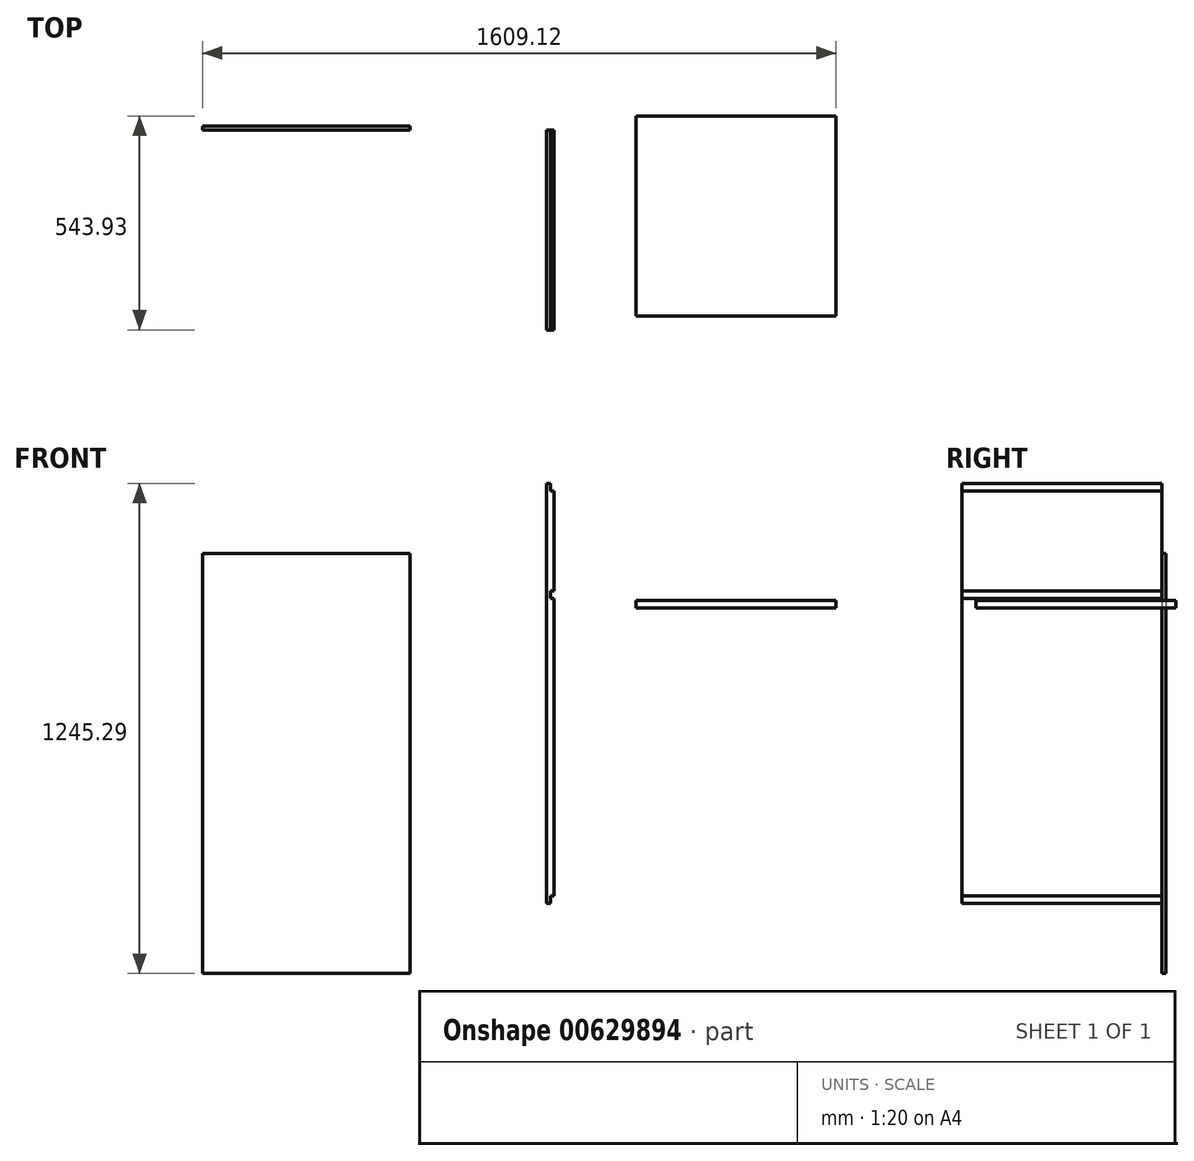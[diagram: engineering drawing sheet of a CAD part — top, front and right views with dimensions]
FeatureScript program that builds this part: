
annotation { "Feature Type Name" : "Feature", "Feature Type Description" : "" }
export const myFeature = defineFeature(function(context is Context, id is Id, definition is map)
    precondition{}
    {
        {
            var Q0;
            Q0=qCreatedBy(makeId("Right.planeOp"),FACE);
            var sketch = newSketch(context, id + "F0", { "sketchPlane" : qUnion([Q0])});
            skLineSegment(sketch, "E0.bottom", {"start": v(-35.93, 999.32) * mm, "end": v(472.07, 999.32) * mm});
            skLineSegment(sketch, "E0.top", {"start": v(-35.93, -67.48) * mm, "end": v(472.07, -67.48) * mm});
            skLineSegment(sketch, "E0.left", {"start": v(-35.93, 999.32) * mm, "end": v(-35.93, -67.48) * mm});
            skLineSegment(sketch, "E0.right", {"start": v(472.07, 999.32) * mm, "end": v(472.07, -67.48) * mm});
            skSolve(sketch);
        }
        {
            var Q0;
            Q0=makeQuery(id+"F0.imprint","IMPRINT",FACE,{"disambiguationData":[TD([[makeQuery(id+"F0.imprint","IMPRINT",EDGE,{"derivedFrom":sQuery(id+"F0.wireOp",EDGE,"E0.bottom")}),-1.0]])]});
            extrude(context, id + "F1", {"entities" : qUnion([Q0]), "depth" : 19.05 * mm, "offsetDistance" : 25.4 * mm});
        }
        {
            var Q0;
            Q0=makeQuery(id+"F1.opExtrude","CAP_FACE",FACE,{"disambiguationData":[OSD([sQuery(id+"F0.wireOp",EDGE,"E0.bottom"),sQuery(id+"F0.wireOp",EDGE,"E0.top"),sQuery(id+"F0.wireOp",EDGE,"E0.left"),sQuery(id+"F0.wireOp",EDGE,"E0.right")])],"isStart":false});
            var sketch = newSketch(context, id + "F2", { "sketchPlane" : qUnion([Q0])});
            skPoint(sketch, "E1.0", {"position": v(-35.93, 999.32) * mm});
            skLineSegment(sketch, "E2.bottom", {"start": v(-35.93, 999.32) * mm, "end": v(472.07, 999.32) * mm});
            skLineSegment(sketch, "E2.top", {"start": v(-35.93, 980.27) * mm, "end": v(472.07, 980.27) * mm});
            skLineSegment(sketch, "E2.left", {"start": v(-35.93, 999.32) * mm, "end": v(-35.93, 980.27) * mm});
            skLineSegment(sketch, "E2.right", {"start": v(472.07, 999.32) * mm, "end": v(472.07, 980.27) * mm});
            skSolve(sketch);
        }
        {
            var Q0;
            Q0=makeQuery(id+"F2.imprint","IMPRINT",FACE,{"disambiguationData":[TD([[makeQuery(id+"F2.imprint","IMPRINT",EDGE,{"derivedFrom":sQuery(id+"F2.wireOp",EDGE,"E2.bottom")}),-1.0]])]});
            extrude(context, id + "F3", {"entities" : qUnion([Q0]), "operationType" : NewBodyOperationType.REMOVE, "oppositeDirection" : true, "depth" : 9.52 * mm, "offsetDistance" : 25.4 * mm});
        }
        {
            var Q0;
            Q0=makeQuery(id+"F1.opExtrude","CAP_FACE",FACE,{"disambiguationData":[OSD([sQuery(id+"F0.wireOp",EDGE,"E0.bottom"),sQuery(id+"F0.wireOp",EDGE,"E0.top"),sQuery(id+"F0.wireOp",EDGE,"E0.left"),sQuery(id+"F0.wireOp",EDGE,"E0.right")])],"isStart":false});
            var sketch = newSketch(context, id + "F4", { "sketchPlane" : qUnion([Q0])});
            skLineSegment(sketch, "E3.bottom", {"start": v(-35.93, -67.48) * mm, "end": v(472.07, -67.48) * mm});
            skLineSegment(sketch, "E3.top", {"start": v(-35.93, -48.43) * mm, "end": v(472.07, -48.43) * mm});
            skLineSegment(sketch, "E3.left", {"start": v(-35.93, -67.48) * mm, "end": v(-35.93, -48.43) * mm});
            skLineSegment(sketch, "E3.right", {"start": v(472.07, -67.48) * mm, "end": v(472.07, -48.43) * mm});
            skSolve(sketch);
        }
        {
            var Q0;
            Q0=makeQuery(id+"F4.imprint","IMPRINT",FACE,{"disambiguationData":[TD([[makeQuery(id+"F4.imprint","IMPRINT",EDGE,{"derivedFrom":sQuery(id+"F4.wireOp",EDGE,"E3.bottom")}),1.0]])]});
            extrude(context, id + "F5", {"entities" : qUnion([Q0]), "operationType" : NewBodyOperationType.REMOVE, "oppositeDirection" : true, "depth" : 9.52 * mm, "offsetDistance" : 25.4 * mm});
        }
        {
            var Q0;
            Q0=makeQuery(id+"F1.opExtrude","CAP_FACE",FACE,{"disambiguationData":[OSD([sQuery(id+"F0.wireOp",EDGE,"E0.bottom"),sQuery(id+"F0.wireOp",EDGE,"E0.top"),sQuery(id+"F0.wireOp",EDGE,"E0.left"),sQuery(id+"F0.wireOp",EDGE,"E0.right")])],"isStart":false});
            var sketch = newSketch(context, id + "F6", { "sketchPlane" : qUnion([Q0])});
            skLineSegment(sketch, "E4.bottom", {"start": v(-35.93, 726.27) * mm, "end": v(472.07, 726.27) * mm});
            skLineSegment(sketch, "E4.top", {"start": v(-35.93, 707.22) * mm, "end": v(472.07, 707.22) * mm});
            skLineSegment(sketch, "E4.left", {"start": v(-35.93, 726.27) * mm, "end": v(-35.93, 707.22) * mm});
            skLineSegment(sketch, "E4.right", {"start": v(472.07, 726.27) * mm, "end": v(472.07, 707.22) * mm});
            skSolve(sketch);
        }
        {
            var Q0;
            Q0=makeQuery(id+"F6.imprint","IMPRINT",FACE,{"disambiguationData":[TD([[makeQuery(id+"F6.imprint","IMPRINT",EDGE,{"derivedFrom":sQuery(id+"F6.wireOp",EDGE,"E4.bottom")}),-1.0]])]});
            extrude(context, id + "F7", {"entities" : qUnion([Q0]), "operationType" : NewBodyOperationType.REMOVE, "oppositeDirection" : true, "depth" : 9.52 * mm, "offsetDistance" : 25.4 * mm});
        }
        {
            var Q0;
            Q0=qCreatedBy(makeId("Front.planeOp"),FACE);
            var sketch = newSketch(context, id + "F8", { "sketchPlane" : qUnion([Q0])});
            skLineSegment(sketch, "E5.bottom", {"start": v(227.33, 682.52) * mm, "end": v(735.33, 682.52) * mm});
            skLineSegment(sketch, "E5.top", {"start": v(227.33, 701.57) * mm, "end": v(735.33, 701.57) * mm});
            skLineSegment(sketch, "E5.left", {"start": v(227.33, 682.52) * mm, "end": v(227.33, 701.57) * mm});
            skLineSegment(sketch, "E5.right", {"start": v(735.33, 682.52) * mm, "end": v(735.33, 701.57) * mm});
            skSolve(sketch);
        }
        {
            var Q0;
            Q0=makeQuery(id+"F8.imprint","IMPRINT",FACE,{"disambiguationData":[TD([[makeQuery(id+"F8.imprint","IMPRINT",EDGE,{"derivedFrom":sQuery(id+"F8.wireOp",EDGE,"E5.bottom")}),1.0]])]});
            extrude(context, id + "F9", {"entities" : qUnion([Q0]), "oppositeDirection" : true, "depth" : 508 * mm, "offsetDistance" : 25.4 * mm});
        }
        {
            var Q0;
            Q0=makeQuery(id+"F1.opExtrude","SWEPT_FACE",FACE,{"disambiguationData":[OSD([sQuery(id+"F0.wireOp",EDGE,"E0.right")])]});
            var sketch = newSketch(context, id + "F10", { "sketchPlane" : qUnion([Q0])});
            skLineSegment(sketch, "E6.bottom", {"start": v(346.74, 820.83) * mm, "end": v(873.8, 820.83) * mm});
            skLineSegment(sketch, "E6.top", {"start": v(346.74, -245.97) * mm, "end": v(873.8, -245.97) * mm});
            skLineSegment(sketch, "E6.left", {"start": v(346.74, 820.83) * mm, "end": v(346.74, -245.97) * mm});
            skLineSegment(sketch, "E6.right", {"start": v(873.8, 820.83) * mm, "end": v(873.8, -245.97) * mm});
            skSolve(sketch);
        }
        {
            var Q0;
            Q0=makeQuery(id+"F10.imprint","IMPRINT",FACE,{"disambiguationData":[TD([[makeQuery(id+"F10.imprint","IMPRINT",EDGE,{"derivedFrom":sQuery(id+"F10.wireOp",EDGE,"E6.bottom")}),-1.0]])]});
            extrude(context, id + "F11", {"entities" : qUnion([Q0]), "depth" : 9.52 * mm, "offsetDistance" : 25.4 * mm});
        }
    });
